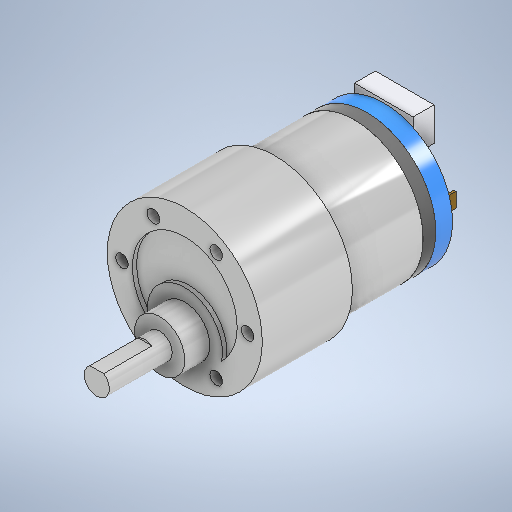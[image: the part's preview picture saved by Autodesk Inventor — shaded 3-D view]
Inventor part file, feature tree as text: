
AUTODESK INVENTOR PART (.ipt)
format: ipt  version: 2025.2 (Build 292293000, 293)  size: 400,384 bytes
history: native  units: mm
features: sketch x14, extrude x13, projected_geometry x1
ambient origin geometry x8: Origin, YZ Plane, XZ Plane, XY Plane, X Axis, Y Axis, Z Axis, Center Point
bodies: Solid1 (feature_tree), Solid2 (feature_tree), Solid3 (feature_tree), Solid4 (feature_tree), Solid5 (feature_tree)
feature tree (28):
  extrude  "Extrusion1"  Depth=21.5mm TaperAngle=0.0deg
  extrude  "Extrusion2"  Depth=19.0mm TaperAngle=0.0deg
  extrude  "Extrusion3"  Depth=6.0mm TaperAngle=0.0deg
  extrude  "Extrusion4"  Depth=15.0mm TaperAngle=0.0deg
  extrude  "Extrusion5"  Depth=11.5mm
  extrude  "Extrusion6"  Depth=60.0mm TaperAngle=360.0deg
  extrude  "Extrusion7"  Depth=3.0mm TaperAngle=0.0deg
  extrude  "Extrusion8"  Depth=4.0mm
  extrude  "Extrusion9"  Depth=1.0mm
  extrude  "Extrusion10"  Depth=1.0mm
  extrude  "Extrusion11"  Depth=1.0mm TaperAngle=0.0deg
  extrude  "Extrusion12"  Depth=8.0mm
  extrude  "Extrusion13"  Depth=5.0mm TaperAngle=0.0deg
  sketch  "Sketch1"  dims[d0=37.0mm d1=21.5mm d2=0.0mm]
  sketch  "Sketch2"  dims[d6=12.0mm d7=6.0mm d8=0.0mm]
  sketch  "Sketch3"  dims[d9=6.0mm d10=15.0mm d11=0.0mm]
  sketch  "Sketch4"  dims[d12=11.5mm d13=0.0mm d14=30.0mm]
  sketch  "Sketch5"  dims[d15=3.0mm d16=60.0mm d18=360.0deg]
  projected_geometry  "Projected Loop1"
  sketch  "Sketch6"  dims[d20=5.0mm d21=0.0mm d22=3.0mm d23=0.0mm]
  sketch  "Sketch Circular Pattern1"  dims[d3=32.8mm d4=19.0mm d5=0.0mm]
  sketch  "Sketch7"  dims[d24=4.0mm d25=0.0mm d26=13.0mm]
  sketch  "Sketch8"  dims[d27=6.5mm d28=0.0mm d29=1.0mm]
  sketch  "Sketch9"  dims[d30=1.0mm d31=0.0mm d32=25.0mm]
  sketch  "Sketch10"  dims[d33=18.0mm d34=1.0mm d35=0.0mm]
  sketch  "Sketch11"  dims[d36=7.0mm d37=8.0mm]
  sketch  "Sketch12"  dims[d38=7.0mm d39=5.0mm d40=0.0mm]
  sketch  "Sketch13"  dims[d41=11.75mm d42=1.75mm d43=0.5mm d44=3.5mm d45=5.0mm d46=0.0mm]
